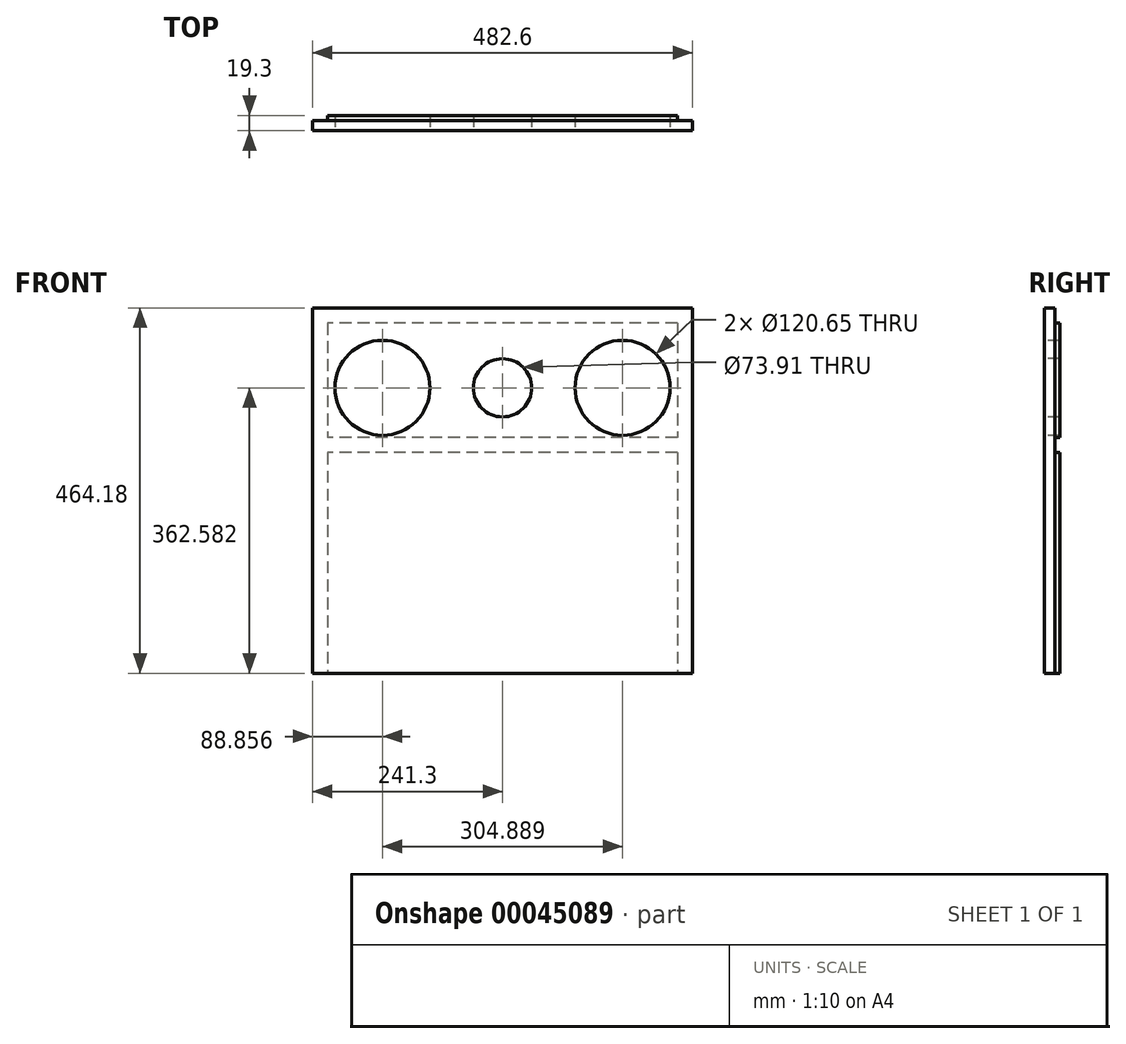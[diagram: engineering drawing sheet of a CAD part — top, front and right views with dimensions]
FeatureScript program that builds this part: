
annotation { "Feature Type Name" : "Feature", "Feature Type Description" : "" }
export const myFeature = defineFeature(function(context is Context, id is Id, definition is map)
    precondition{}
    {
        {
            var Q0;
            Q0=qCreatedBy(makeId("Front.planeOp"),FACE);
            var sketch = newSketch(context, id + "F0", { "sketchPlane" : qUnion([Q0])});
            skLineSegment(sketch, "E0.rect.bottom", {"start": v(-241.3, 232.1) * mm, "end": v(241.3, 232.1) * mm});
            skLineSegment(sketch, "E0.rect.top", {"start": v(-241.3, -232.1) * mm, "end": v(241.3, -232.1) * mm});
            skLineSegment(sketch, "E0.rect.left", {"start": v(-241.3, 232.1) * mm, "end": v(-241.3, -232.1) * mm});
            skLineSegment(sketch, "E0.rect.right", {"start": v(241.3, 232.1) * mm, "end": v(241.3, -232.1) * mm});
            skPoint(sketch, "E0.rect.middle", {"position": v(0, 0) * mm});
            skSolve(sketch);
        }
        {
            var Q0;
            Q0 = qSketchRegion(id + "F0", true);
            extrude(context, id + "F1", {"entities" : qUnion([Q0]), "depth" : 19.3 * mm});
        }
        {
            var Q0;
            Q0=makeQuery(id+"F1.opExtrude","CAP_FACE",FACE,{"disambiguationData":[OSD([sQuery(id+"F0.wireOp",EDGE,"E0.rect.bottom"),sQuery(id+"F0.wireOp",EDGE,"E0.rect.top"),sQuery(id+"F0.wireOp",EDGE,"E0.rect.left"),sQuery(id+"F0.wireOp",EDGE,"E0.rect.right")])],"isStart":false});
            var sketch = newSketch(context, id + "F2", { "sketchPlane" : qUnion([Q0])});
            skLineSegment(sketch, "E1", {"start": v(0, 232.1) * mm, "end": v(0, -232.1) * mm, "construction": true});
            skLineSegment(sketch, "E2", {"start": v(-241.3, 130.5) * mm, "end": v(241.3, 130.5) * mm, "construction": true});
            skPoint(sketch, "E3", {"position": v(-152.44, 130.5) * mm});
            skPoint(sketch, "E4", {"position": v(0, 130.5) * mm});
            skPoint(sketch, "E5.MirrorP", {"position": v(152.44, 130.5) * mm});
            skSolve(sketch);
        }
        {
            var Q0;
            Q0=sQuery(id+"F2.wireOp",VERTEX,"E4");
            var Q1;
            Q1=makeQuery(id+"F1.opExtrude","SWEPT_BODY",BODY,{"disambiguationData":[OSD([sQuery(id+"F0.wireOp",EDGE,"E0.rect.bottom"),sQuery(id+"F0.wireOp",EDGE,"E0.rect.top"),sQuery(id+"F0.wireOp",EDGE,"E0.rect.left"),sQuery(id+"F0.wireOp",EDGE,"E0.rect.right")])]});
            hole(context, id + "F3", {"style" : HoleStyle.SIMPLE, "holeDiameter" : 73.9 * mm, "endStyle" : HoleEndStyle.THROUGH, "locations" : qUnion([Q0]), "scope" : qUnion([Q1])});
        }
        {
            var Q0;
            Q0=sQuery(id+"F2.wireOp",VERTEX,"E3");
            var Q1;
            Q1=sQuery(id+"F2.wireOp",VERTEX,"E5.MirrorP");
            var Q2;
            Q2=makeQuery(id+"F1.opExtrude","SWEPT_BODY",BODY,{"disambiguationData":[OSD([sQuery(id+"F0.wireOp",EDGE,"E0.rect.bottom"),sQuery(id+"F0.wireOp",EDGE,"E0.rect.top"),sQuery(id+"F0.wireOp",EDGE,"E0.rect.left"),sQuery(id+"F0.wireOp",EDGE,"E0.rect.right")])]});
            hole(context, id + "F4", {"style" : HoleStyle.SIMPLE, "holeDiameter" : 120.65 * mm, "endStyle" : HoleEndStyle.THROUGH, "locations" : qUnion([Q0, Q1]), "scope" : qUnion([Q2])});
        }
        {
            var Q0;
            Q0=makeQuery(id+"F1.opExtrude","CAP_FACE",FACE,{"disambiguationData":[OSD([sQuery(id+"F0.wireOp",EDGE,"E0.rect.bottom"),sQuery(id+"F0.wireOp",EDGE,"E0.rect.top"),sQuery(id+"F0.wireOp",EDGE,"E0.rect.left"),sQuery(id+"F0.wireOp",EDGE,"E0.rect.right")])],"isStart":true});
            var sketch = newSketch(context, id + "F5", { "sketchPlane" : qUnion([Q0])});
            skLineSegment(sketch, "E6.bottom", {"start": v(-241.3, 232.1) * mm, "end": v(-222, 232.1) * mm});
            skLineSegment(sketch, "E6.top", {"start": v(-241.3, -232.1) * mm, "end": v(-222, -232.1) * mm});
            skLineSegment(sketch, "E6.left", {"start": v(-241.3, 232.1) * mm, "end": v(-241.3, -232.1) * mm});
            skLineSegment(sketch, "E6.right", {"start": v(-222, 232.1) * mm, "end": v(-222, -232.1) * mm});
            skLineSegment(sketch, "E7.bottom", {"start": v(241.3, 232.1) * mm, "end": v(222, 232.1) * mm});
            skLineSegment(sketch, "E7.top", {"start": v(241.3, -232.1) * mm, "end": v(222, -232.1) * mm});
            skLineSegment(sketch, "E7.left", {"start": v(241.3, 232.1) * mm, "end": v(241.3, -232.1) * mm});
            skLineSegment(sketch, "E7.right", {"start": v(222, 232.1) * mm, "end": v(222, -232.1) * mm});
            skLineSegment(sketch, "E8.bottom", {"start": v(-241.3, 232.1) * mm, "end": v(241.3, 232.1) * mm});
            skLineSegment(sketch, "E8.top", {"start": v(-241.3, 212.79) * mm, "end": v(241.3, 212.79) * mm});
            skLineSegment(sketch, "E8.left", {"start": v(-241.3, 232.1) * mm, "end": v(-241.3, 212.79) * mm});
            skLineSegment(sketch, "E8.right", {"start": v(241.3, 232.1) * mm, "end": v(241.3, 212.79) * mm});
            skLineSegment(sketch, "E9.bottom", {"start": v(-241.3, 67.37) * mm, "end": v(241.3, 67.37) * mm});
            skLineSegment(sketch, "E9.top", {"start": v(-241.3, 48.07) * mm, "end": v(241.3, 48.07) * mm});
            skLineSegment(sketch, "E9.left", {"start": v(-241.3, 67.37) * mm, "end": v(-241.3, 48.07) * mm});
            skLineSegment(sketch, "E9.right", {"start": v(241.3, 67.37) * mm, "end": v(241.3, 48.07) * mm});
            skSolve(sketch);
        }
        {
            var Q0;
            Q0 = qSketchRegion(id + "F5", true);
            extrude(context, id + "F6", {"entities" : qUnion([Q0]), "operationType" : NewBodyOperationType.REMOVE, "oppositeDirection" : true, "depth" : 6.35 * mm});
        }
    });
